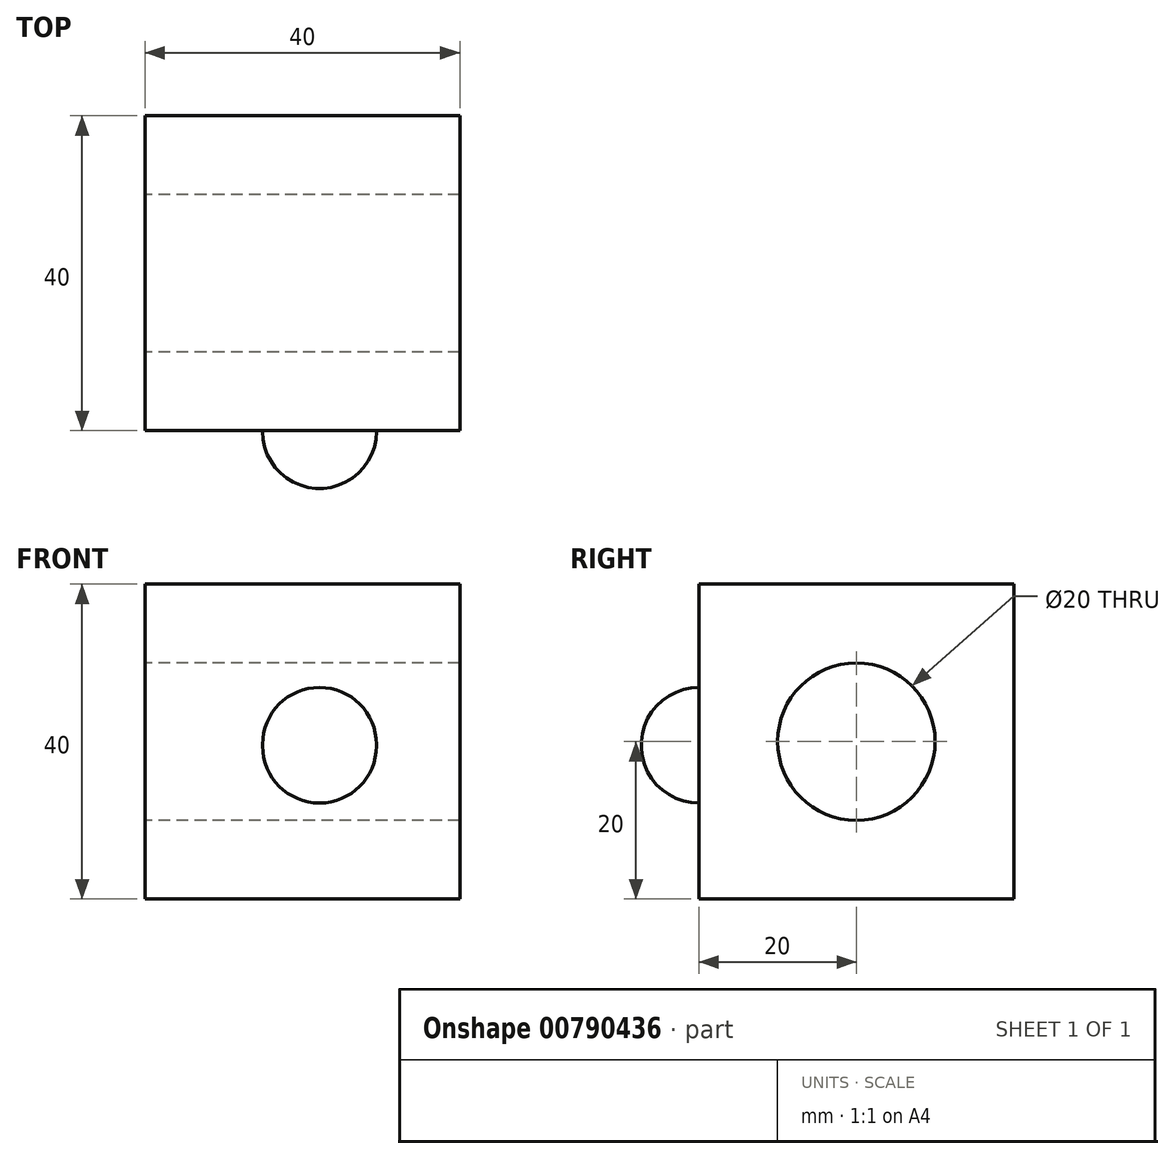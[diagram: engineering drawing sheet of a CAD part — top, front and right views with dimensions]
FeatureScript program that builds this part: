
annotation { "Feature Type Name" : "Feature", "Feature Type Description" : "" }
export const myFeature = defineFeature(function(context is Context, id is Id, definition is map)
    precondition{}
    {
        {
            var Q0;
            Q0=qCreatedBy(makeId("Front.planeOp"),FACE);
            var sketch = newSketch(context, id + "F0", { "sketchPlane" : qUnion([Q0])});
            skLineSegment(sketch, "E0.bottom", {"start": v(40, 40) * mm, "end": v(0, 40) * mm});
            skLineSegment(sketch, "E0.top", {"start": v(40, 0) * mm, "end": v(0, 0) * mm});
            skLineSegment(sketch, "E0.left", {"start": v(40, 40) * mm, "end": v(40, 0) * mm});
            skLineSegment(sketch, "E0.right", {"start": v(0, 40) * mm, "end": v(0, 0) * mm});
            skSolve(sketch);
        }
        {
            var Q0;
            Q0 = qSketchRegion(id + "F0", true);
            extrude(context, id + "F1", {"entities" : qUnion([Q0]), "depth" : 40 * mm, "offsetDistance" : 25 * mm});
        }
        {
            var Q0;
            Q0=makeQuery(id+"F1.opExtrude","SWEPT_FACE",FACE,{"disambiguationData":[OSD([sQuery(id+"F0.wireOp",EDGE,"E0.right")])]});
            var sketch = newSketch(context, id + "F2", { "sketchPlane" : qUnion([Q0])});
            skCircle(sketch, "E1", {"center": v(20, 20) * mm, "radius": 10 * mm});
            skPoint(sketch, "E1.centerSnap0", {"position": v(40, 20) * mm});
            skPoint(sketch, "E1.centerSnap1", {"position": v(20, 40) * mm});
            skSolve(sketch);
        }
        {
            var Q0;
            Q0 = qSketchRegion(id + "F2", true);
            extrude(context, id + "F3", {"entities" : qUnion([Q0]), "operationType" : NewBodyOperationType.REMOVE, "endBound" : BoundingType.THROUGH_ALL, "oppositeDirection" : true, "depth" : 25 * mm, "offsetDistance" : 25 * mm});
        }
        {
            var Q0;
            Q0=makeQuery(id+"F1.opExtrude","CAP_FACE",FACE,{"disambiguationData":[OSD([sQuery(id+"F0.wireOp",EDGE,"E0.bottom"),sQuery(id+"F0.wireOp",EDGE,"E0.top"),sQuery(id+"F0.wireOp",EDGE,"E0.left"),sQuery(id+"F0.wireOp",EDGE,"E0.right")])],"isStart":false});
            var sketch = newSketch(context, id + "F4", { "sketchPlane" : qUnion([Q0])});
            skLineSegment(sketch, "E2", {"start": v(14.93, 19.54) * mm, "end": v(29.4, 19.54) * mm});
            skArc(sketch, "E3", {"start": v(29.4, 19.54) * mm, "mid": v(22.16, 26.89) * mm, "end": v(14.93, 19.54) * mm});
            skSolve(sketch);
        }
        {
            var Q0;
            Q0=makeQuery(id+"F4.imprint","IMPRINT",FACE,{"disambiguationData":[TD([[makeQuery(id+"F4.imprint","IMPRINT",EDGE,{"derivedFrom":sQuery(id+"F4.wireOp",EDGE,"E2")}),1.0]])]});
            var Q1;
            Q1=sQuery(id+"F4.wireOp",EDGE,"E2");
            revolve(context, id + "F5", {"operationType" : NewBodyOperationType.ADD, "surfaceOperationType" : NewSurfaceOperationType.NEW, "entities" : qUnion([Q0]), "axis" : qUnion([Q1]), "revolveType" : RevolveType.FULL});
        }
    });
